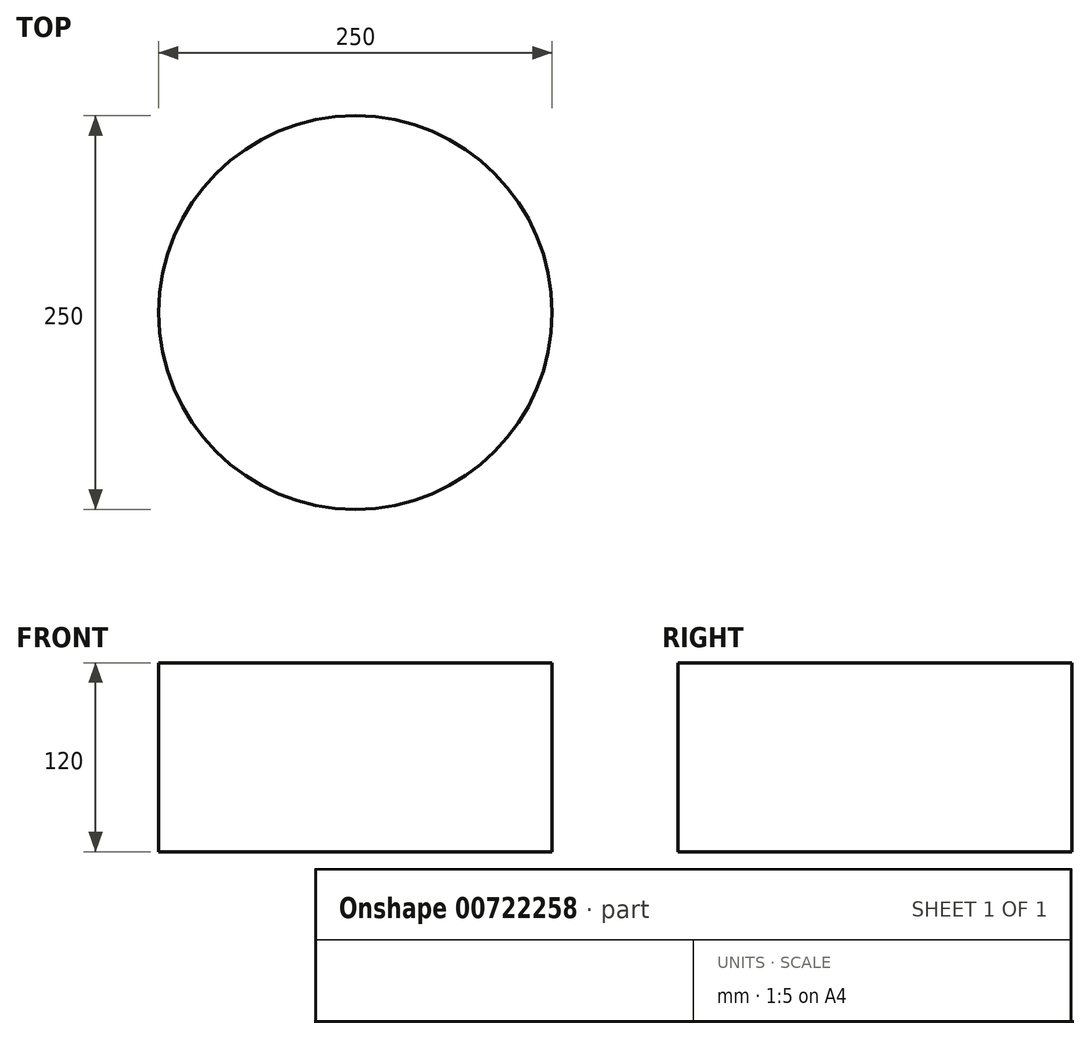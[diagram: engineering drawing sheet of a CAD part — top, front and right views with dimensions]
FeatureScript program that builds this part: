
annotation { "Feature Type Name" : "Feature", "Feature Type Description" : "" }
export const myFeature = defineFeature(function(context is Context, id is Id, definition is map)
    precondition{}
    {
        {
            var Q0;
            Q0=qCreatedBy(makeId("Top.planeOp"),FACE);
            var sketch = newSketch(context, id + "F0", { "sketchPlane" : qUnion([Q0])});
            skCircle(sketch, "E0", {"center": v(0, 0) * mm, "radius": 125 * mm});
            skSolve(sketch);
        }
        {
            var Q0;
            Q0=makeQuery(id+"F0.imprint","IMPRINT",FACE,{"disambiguationData":[TD([[makeQuery(id+"F0.imprint","IMPRINT",EDGE,{"derivedFrom":sQuery(id+"F0.wireOp",EDGE,"E0")}),1.0]])]});
            extrude(context, id + "F1", {"entities" : qUnion([Q0]), "depth" : 120 * mm, "offsetDistance" : 25 * mm});
        }
    });
